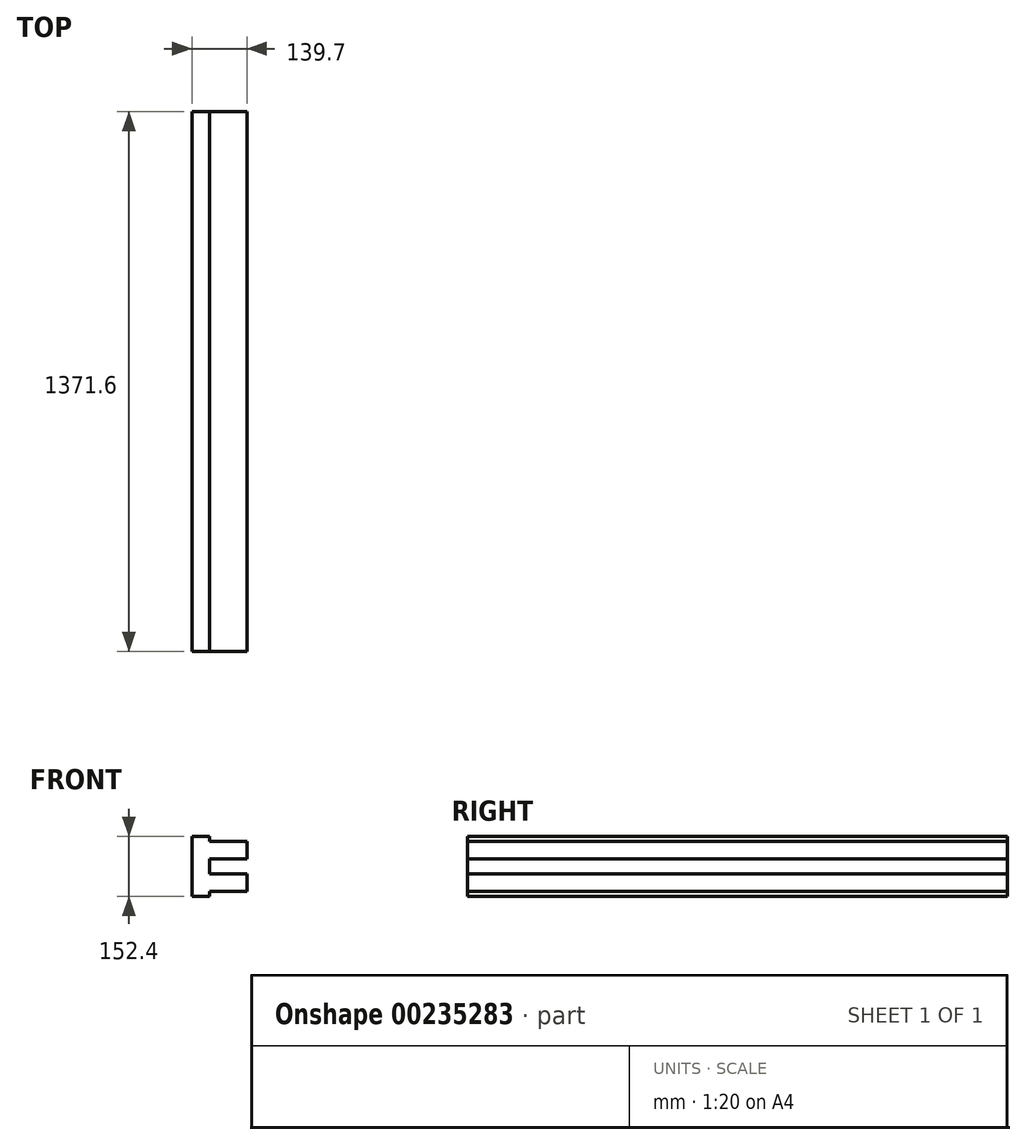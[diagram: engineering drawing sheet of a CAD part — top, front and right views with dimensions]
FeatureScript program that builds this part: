
annotation { "Feature Type Name" : "Feature", "Feature Type Description" : "" }
export const myFeature = defineFeature(function(context is Context, id is Id, definition is map)
    precondition{}
    {
        {
            var Q0;
            Q0=qCreatedBy(makeId("Front.planeOp"),FACE);
            var sketch = newSketch(context, id + "F0", { "sketchPlane" : qUnion([Q0])});
            skLineSegment(sketch, "E0", {"start": v(0, 0) * mm, "end": v(44.45, 0) * mm});
            skLineSegment(sketch, "E1", {"start": v(44.45, 0) * mm, "end": v(44.45, 152.4) * mm});
            skLineSegment(sketch, "E2", {"start": v(44.45, 152.4) * mm, "end": v(0, 152.4) * mm});
            skLineSegment(sketch, "E3", {"start": v(0, 152.4) * mm, "end": v(0, 0) * mm});
            skSolve(sketch);
        }
        {
            var Q0;
            Q0=makeQuery(id+"F0.imprint","IMPRINT",FACE,{"disambiguationData":[TD([[makeQuery(id+"F0.imprint","IMPRINT",EDGE,{"derivedFrom":sQuery(id+"F0.wireOp",EDGE,"E0")}),1.0]])]});
            extrude(context, id + "F1", {"entities" : qUnion([Q0]), "depth" : 1371.6 * mm});
        }
        {
            var Q0;
            Q0=makeQuery(id+"F1.opExtrude","SWEPT_FACE",FACE,{"disambiguationData":[OSD([sQuery(id+"F0.wireOp",EDGE,"E1")])]});
            var sketch = newSketch(context, id + "F2", { "sketchPlane" : qUnion([Q0])});
            skLineSegment(sketch, "E4", {"start": v(-1371.6, 152.4) * mm, "end": v(-1371.6, 139.7) * mm});
            skLineSegment(sketch, "E5", {"start": v(-1371.6, 139.7) * mm, "end": v(0, 139.7) * mm});
            skLineSegment(sketch, "E6", {"start": v(0, 139.7) * mm, "end": v(0, 95.25) * mm});
            skLineSegment(sketch, "E7", {"start": v(0, 95.25) * mm, "end": v(-1371.6, 95.25) * mm});
            skLineSegment(sketch, "E8", {"start": v(-1371.6, 76.2) * mm, "end": v(-1340.65, 76.2) * mm});
            skLineSegment(sketch, "E9.MirrorCS", {"start": v(0, 57.15) * mm, "end": v(-1371.6, 57.15) * mm});
            skLineSegment(sketch, "E10.MirrorCS", {"start": v(-1371.6, 12.7) * mm, "end": v(0, 12.7) * mm});
            skSolve(sketch);
        }
        {
            var Q0;
            {var subQ0=sQuery(id+"F2.wireOp",EDGE,"E5");Q0=makeQuery(id+"F2.imprint","IMPRINT",FACE,{"disambiguationData":[TD([[makeQuery(id+"F2.imprint","IMPRINT",EDGE,{"derivedFrom":subQ0}),-1.0]])]});}
            var Q1;
            {var subQ0=sQuery(id+"F2.wireOp",EDGE,"E9.MirrorCS");Q1=makeQuery(id+"F2.imprint","IMPRINT",FACE,{"disambiguationData":[TD([[makeQuery(id+"F2.imprint","IMPRINT",EDGE,{"derivedFrom":subQ0}),1.0]])]});}
            extrude(context, id + "F3", {"entities" : qUnion([Q0, Q1]), "operationType" : NewBodyOperationType.ADD, "depth" : 95.25 * mm});
        }
    });
